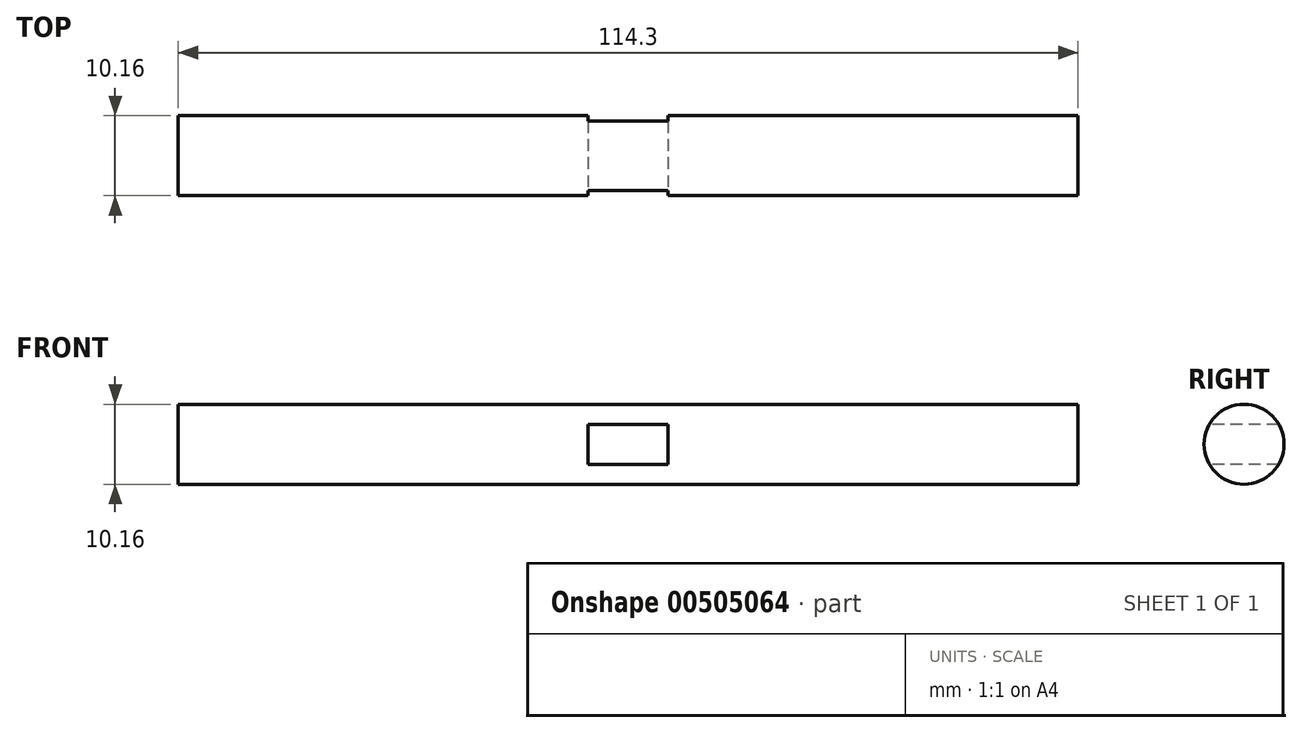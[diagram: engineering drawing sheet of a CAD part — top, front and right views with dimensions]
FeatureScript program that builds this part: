
annotation { "Feature Type Name" : "Feature", "Feature Type Description" : "" }
export const myFeature = defineFeature(function(context is Context, id is Id, definition is map)
    precondition{}
    {
        {
            var Q0;
            Q0=qCreatedBy(makeId("Front.planeOp"),FACE);
            var sketch = newSketch(context, id + "F0", { "sketchPlane" : qUnion([Q0])});
            skLineSegment(sketch, "E0.bottom", {"start": v(-57.15, 5.08) * mm, "end": v(57.15, 5.08) * mm});
            skLineSegment(sketch, "E0.top", {"start": v(-57.15, 0) * mm, "end": v(57.15, 0) * mm});
            skLineSegment(sketch, "E0.left", {"start": v(-57.15, 5.08) * mm, "end": v(-57.15, 0) * mm});
            skLineSegment(sketch, "E0.right", {"start": v(57.15, 5.08) * mm, "end": v(57.15, 0) * mm});
            skSolve(sketch);
        }
        {
            var Q0;
            Q0=makeQuery(id+"F0.imprint","IMPRINT",FACE,{"disambiguationData":[TD([[makeQuery(id+"F0.imprint","IMPRINT",EDGE,{"derivedFrom":sQuery(id+"F0.wireOp",EDGE,"E0.bottom")}),-1.0]])]});
            var Q1;
            Q1=sQuery(id+"F0.wireOp",EDGE,"E0.top");
            revolve(context, id + "F1", {"entities" : qUnion([Q0]), "axis" : qUnion([Q1]), "revolveType" : RevolveType.FULL});
        }
        {
            var Q0;
            Q0=qCreatedBy(makeId("Front.planeOp"),FACE);
            var sketch = newSketch(context, id + "F2", { "sketchPlane" : qUnion([Q0])});
            skLineSegment(sketch, "E1.bottom", {"start": v(-5.08, 2.54) * mm, "end": v(5.08, 2.54) * mm});
            skLineSegment(sketch, "E1.top", {"start": v(-5.08, -2.54) * mm, "end": v(5.08, -2.54) * mm});
            skLineSegment(sketch, "E1.left", {"start": v(-5.08, 2.54) * mm, "end": v(-5.08, -2.54) * mm});
            skLineSegment(sketch, "E1.right", {"start": v(5.08, 2.54) * mm, "end": v(5.08, -2.54) * mm});
            skSolve(sketch);
        }
        {
            var Q0;
            Q0 = qSketchRegion(id + "F2", true);
            extrude(context, id + "F3", {"entities" : qUnion([Q0]), "operationType" : NewBodyOperationType.REMOVE, "endBound" : BoundingType.SYMMETRIC, "oppositeDirection" : true, "depth" : 25.4 * mm});
        }
    });
